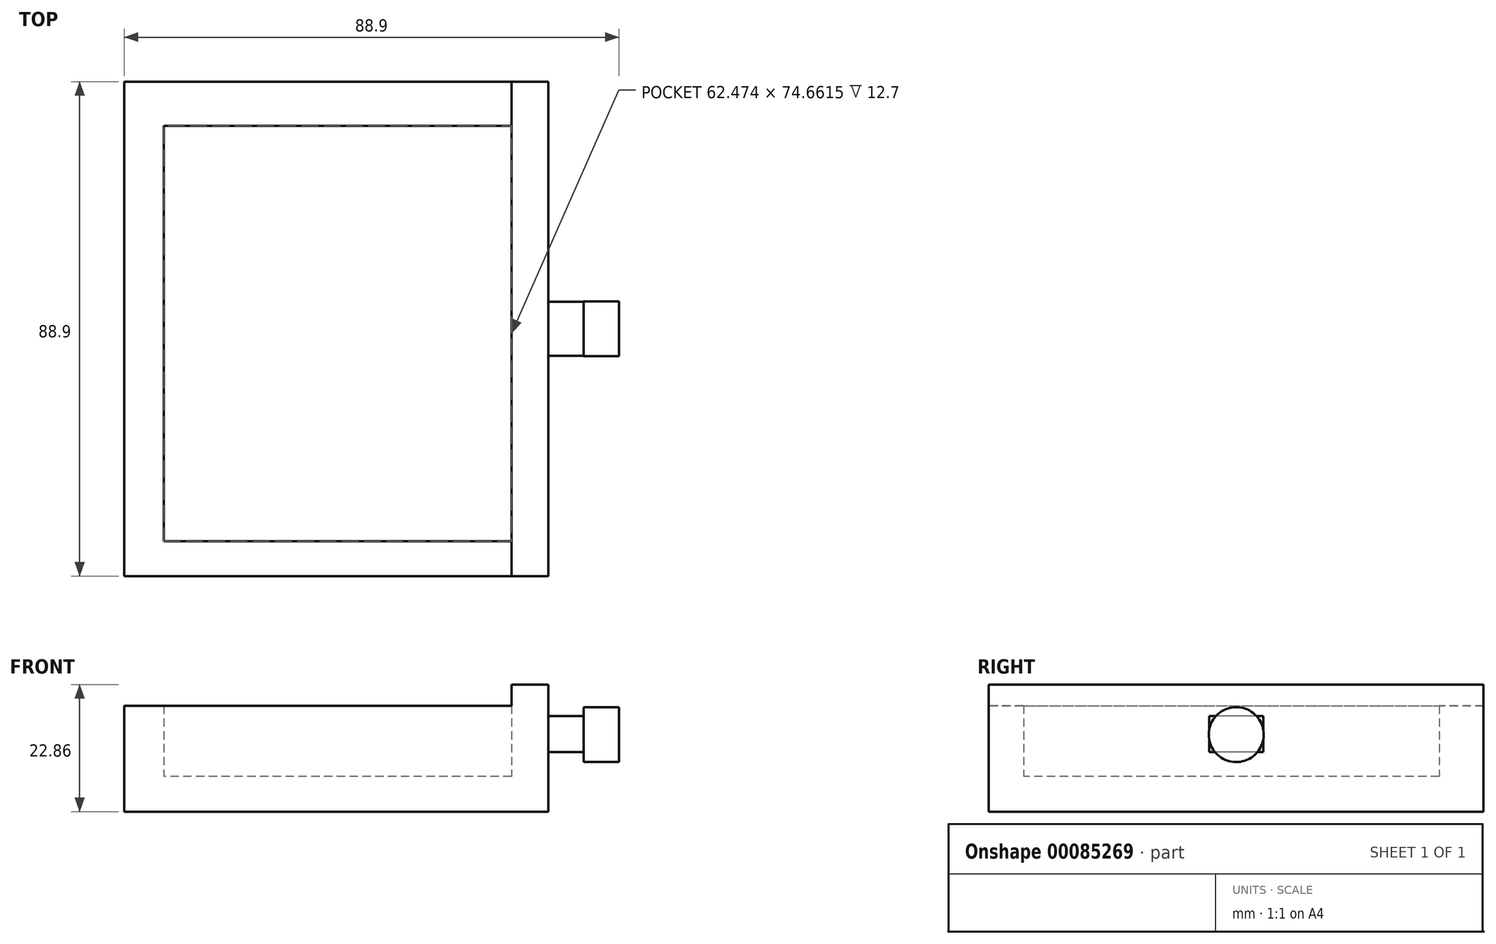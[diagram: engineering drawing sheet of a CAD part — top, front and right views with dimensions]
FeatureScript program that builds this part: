
annotation { "Feature Type Name" : "Feature", "Feature Type Description" : "" }
export const myFeature = defineFeature(function(context is Context, id is Id, definition is map)
    precondition{}
    {
        {
            var Q0;
            Q0=qCreatedBy(makeId("Top.planeOp"),FACE);
            var sketch = newSketch(context, id + "F0", { "sketchPlane" : qUnion([Q0])});
            skLineSegment(sketch, "E0.bottom", {"start": v(38.1, -44.45) * mm, "end": v(-38.1, -44.45) * mm});
            skLineSegment(sketch, "E0.top", {"start": v(38.1, 44.45) * mm, "end": v(-38.1, 44.45) * mm});
            skLineSegment(sketch, "E0.left", {"start": v(38.1, -44.45) * mm, "end": v(38.1, 44.45) * mm});
            skLineSegment(sketch, "E0.right", {"start": v(-38.1, -44.45) * mm, "end": v(-38.1, 44.45) * mm});
            skPoint(sketch, "E0.middle", {"position": v(0, 0) * mm});
            skSolve(sketch);
        }
        {
            var Q0;
            Q0=makeQuery(id+"F0.imprint","IMPRINT",FACE,{"disambiguationData":[TD([[makeQuery(id+"F0.imprint","IMPRINT",EDGE,{"derivedFrom":sQuery(id+"F0.wireOp",EDGE,"E0.bottom")}),-1.0]])]});
            extrude(context, id + "F1", {"entities" : qUnion([Q0]), "depth" : 6.35 * mm});
        }
        {
            var Q0;
            Q0=makeQuery(id+"F1.opExtrude","CAP_FACE",FACE,{"disambiguationData":[OSD([sQuery(id+"F0.wireOp",EDGE,"E0.bottom"),sQuery(id+"F0.wireOp",EDGE,"E0.top"),sQuery(id+"F0.wireOp",EDGE,"E0.left"),sQuery(id+"F0.wireOp",EDGE,"E0.right")])],"isStart":false});
            var sketch = newSketch(context, id + "F2", { "sketchPlane" : qUnion([Q0])});
            skLineSegment(sketch, "E1.bottom", {"start": v(38.1, 44.45) * mm, "end": v(31.49, 44.45) * mm});
            skLineSegment(sketch, "E1.top", {"start": v(38.1, -44.45) * mm, "end": v(31.49, -44.45) * mm});
            skLineSegment(sketch, "E1.left", {"start": v(38.1, 44.45) * mm, "end": v(38.1, -44.45) * mm});
            skLineSegment(sketch, "E1.right", {"start": v(31.49, 44.45) * mm, "end": v(31.49, -44.45) * mm});
            skSolve(sketch);
        }
        {
            var Q0;
            Q0=makeQuery(id+"F2.imprint","IMPRINT",FACE,{"disambiguationData":[TD([[makeQuery(id+"F2.imprint","IMPRINT",EDGE,{"derivedFrom":sQuery(id+"F2.wireOp",EDGE,"E1.bottom")}),1.0]])]});
            extrude(context, id + "F3", {"entities" : qUnion([Q0]), "operationType" : NewBodyOperationType.ADD, "depth" : 16.5 * mm});
        }
        {
            var Q0;
            Q0=makeQuery(id+"F1.opExtrude","CAP_FACE",FACE,{"disambiguationData":[OSD([sQuery(id+"F0.wireOp",EDGE,"E0.bottom"),sQuery(id+"F0.wireOp",EDGE,"E0.top"),sQuery(id+"F0.wireOp",EDGE,"E0.left"),sQuery(id+"F0.wireOp",EDGE,"E0.right")])],"isStart":false});
            var sketch = newSketch(context, id + "F4", { "sketchPlane" : qUnion([Q0])});
            skLineSegment(sketch, "E2.bottom", {"start": v(31.49, -44.45) * mm, "end": v(-38.1, -44.45) * mm});
            skLineSegment(sketch, "E2.top", {"start": v(31.49, -38.17) * mm, "end": v(-38.1, -38.17) * mm});
            skLineSegment(sketch, "E2.left", {"start": v(31.49, -44.45) * mm, "end": v(31.49, -38.17) * mm});
            skLineSegment(sketch, "E2.right", {"start": v(-38.1, -44.45) * mm, "end": v(-38.1, -38.17) * mm});
            skSolve(sketch);
        }
        {
            var Q0;
            Q0=makeQuery(id+"F4.imprint","IMPRINT",FACE,{"disambiguationData":[TD([[makeQuery(id+"F4.imprint","IMPRINT",EDGE,{"derivedFrom":sQuery(id+"F4.wireOp",EDGE,"E2.bottom")}),-1.0]])]});
            extrude(context, id + "F5", {"entities" : qUnion([Q0]), "operationType" : NewBodyOperationType.ADD, "depth" : 12.7 * mm});
        }
        {
            var Q0;
            Q0=makeQuery(id+"F1.opExtrude","CAP_FACE",FACE,{"disambiguationData":[OSD([sQuery(id+"F0.wireOp",EDGE,"E0.bottom"),sQuery(id+"F0.wireOp",EDGE,"E0.top"),sQuery(id+"F0.wireOp",EDGE,"E0.left"),sQuery(id+"F0.wireOp",EDGE,"E0.right")])],"isStart":false});
            var sketch = newSketch(context, id + "F6", { "sketchPlane" : qUnion([Q0])});
            skLineSegment(sketch, "E3.bottom", {"start": v(-38.1, -38.17) * mm, "end": v(-30.99, -38.17) * mm});
            skLineSegment(sketch, "E3.top", {"start": v(-38.1, 44.45) * mm, "end": v(-30.99, 44.45) * mm});
            skLineSegment(sketch, "E3.left", {"start": v(-38.1, -38.17) * mm, "end": v(-38.1, 44.45) * mm});
            skLineSegment(sketch, "E3.right", {"start": v(-30.99, -38.17) * mm, "end": v(-30.99, 44.45) * mm});
            skSolve(sketch);
        }
        {
            var Q0;
            Q0=makeQuery(id+"F6.imprint","IMPRINT",FACE,{"disambiguationData":[TD([[makeQuery(id+"F6.imprint","IMPRINT",EDGE,{"derivedFrom":sQuery(id+"F6.wireOp",EDGE,"E3.bottom")}),-1.0]])]});
            extrude(context, id + "F7", {"entities" : qUnion([Q0]), "operationType" : NewBodyOperationType.ADD, "depth" : 12.7 * mm});
        }
        {
            var Q0;
            Q0=makeQuery(id+"F1.opExtrude","CAP_FACE",FACE,{"disambiguationData":[OSD([sQuery(id+"F0.wireOp",EDGE,"E0.bottom"),sQuery(id+"F0.wireOp",EDGE,"E0.top"),sQuery(id+"F0.wireOp",EDGE,"E0.left"),sQuery(id+"F0.wireOp",EDGE,"E0.right")])],"isStart":false});
            var sketch = newSketch(context, id + "F8", { "sketchPlane" : qUnion([Q0])});
            skLineSegment(sketch, "E4.bottom", {"start": v(31.49, 44.45) * mm, "end": v(-30.99, 44.45) * mm});
            skLineSegment(sketch, "E4.top", {"start": v(31.49, 36.49) * mm, "end": v(-30.99, 36.49) * mm});
            skLineSegment(sketch, "E4.left", {"start": v(31.49, 44.45) * mm, "end": v(31.49, 36.49) * mm});
            skLineSegment(sketch, "E4.right", {"start": v(-30.99, 44.45) * mm, "end": v(-30.99, 36.49) * mm});
            skSolve(sketch);
        }
        {
            var Q0;
            Q0=makeQuery(id+"F8.imprint","IMPRINT",FACE,{"disambiguationData":[TD([[makeQuery(id+"F8.imprint","IMPRINT",EDGE,{"derivedFrom":sQuery(id+"F8.wireOp",EDGE,"E4.bottom")}),1.0]])]});
            extrude(context, id + "F9", {"entities" : qUnion([Q0]), "operationType" : NewBodyOperationType.ADD, "depth" : 12.7 * mm});
        }
        {
            var Q0;
            Q0=makeQuery(id+"F3.boolean.opBoolean","MERGE",FACE,{"derivedFrom":[makeQuery(id+"F1.opExtrude","SWEPT_FACE",FACE,{"disambiguationData":[OSD([sQuery(id+"F0.wireOp",EDGE,"E0.left")])]}),makeQuery(id+"F3.opExtrude","SWEPT_FACE",FACE,{"disambiguationData":[OSD([sQuery(id+"F2.wireOp",EDGE,"E1.left")])]})]});
            var sketch = newSketch(context, id + "F10", { "sketchPlane" : qUnion([Q0])});
            skLineSegment(sketch, "E5.bottom", {"start": v(4.87, 10.72) * mm, "end": v(-4.87, 10.72) * mm});
            skLineSegment(sketch, "E5.top", {"start": v(4.87, 17.16) * mm, "end": v(-4.87, 17.16) * mm});
            skLineSegment(sketch, "E5.left", {"start": v(4.87, 10.72) * mm, "end": v(4.87, 17.16) * mm});
            skLineSegment(sketch, "E5.right", {"start": v(-4.87, 10.72) * mm, "end": v(-4.87, 17.16) * mm});
            skPoint(sketch, "E5.middle", {"position": v(0, 13.94) * mm});
            skSolve(sketch);
        }
        {
            var Q0;
            Q0=makeQuery(id+"F10.imprint","IMPRINT",FACE,{"disambiguationData":[TD([[makeQuery(id+"F10.imprint","IMPRINT",EDGE,{"derivedFrom":sQuery(id+"F10.wireOp",EDGE,"E5.bottom")}),-1.0]])]});
            extrude(context, id + "F11", {"entities" : qUnion([Q0]), "operationType" : NewBodyOperationType.ADD, "depth" : 6.35 * mm});
        }
        {
            var Q0;
            Q0=makeQuery(id+"F11.opExtrude","CAP_FACE",FACE,{"disambiguationData":[OSD([sQuery(id+"F10.wireOp",EDGE,"E5.bottom"),sQuery(id+"F10.wireOp",EDGE,"E5.top"),sQuery(id+"F10.wireOp",EDGE,"E5.left"),sQuery(id+"F10.wireOp",EDGE,"E5.right")])],"isStart":false});
            var sketch = newSketch(context, id + "F12", { "sketchPlane" : qUnion([Q0])});
            skCircle(sketch, "E6", {"center": v(0, 13.84) * mm, "radius": 4.94 * mm});
            skSolve(sketch);
        }
        {
            var Q0;
            Q0 = qSketchRegion(id + "F12", true);
            extrude(context, id + "F13", {"entities" : qUnion([Q0]), "operationType" : NewBodyOperationType.ADD, "depth" : 6.35 * mm});
        }
    });
